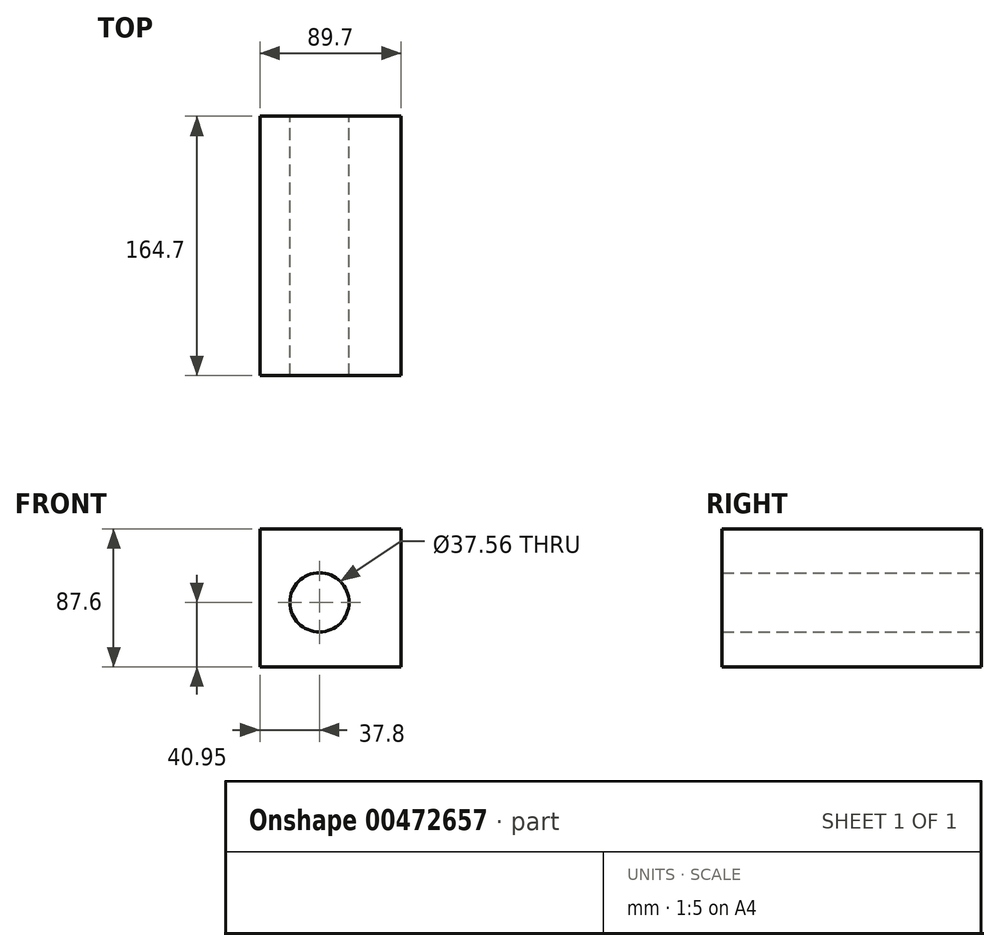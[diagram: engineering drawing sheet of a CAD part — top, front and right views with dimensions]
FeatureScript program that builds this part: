
annotation { "Feature Type Name" : "Feature", "Feature Type Description" : "" }
export const myFeature = defineFeature(function(context is Context, id is Id, definition is map)
    precondition{}
    {
        {
            var Q0;
            Q0=qCreatedBy(makeId("Front.planeOp"),FACE);
            var sketch = newSketch(context, id + "F0", { "sketchPlane" : qUnion([Q0])});
            skLineSegment(sketch, "E0.bottom", {"start": v(-40.5, 46.65) * mm, "end": v(49.2, 46.65) * mm});
            skLineSegment(sketch, "E0.top", {"start": v(-40.5, -40.95) * mm, "end": v(49.2, -40.95) * mm});
            skLineSegment(sketch, "E0.left", {"start": v(-40.5, 46.65) * mm, "end": v(-40.5, -40.95) * mm});
            skLineSegment(sketch, "E0.right", {"start": v(49.2, 46.65) * mm, "end": v(49.2, -40.95) * mm});
            skCircle(sketch, "E1", {"center": v(-2.7, 0) * mm, "radius": 18.78 * mm});
            skSolve(sketch);
        }
        {
            var Q0;
            Q0 = qSketchRegion(id + "F0", true);
            extrude(context, id + "F1", {"entities" : qUnion([Q0]), "depth" : 164.7 * mm});
        }
    });
